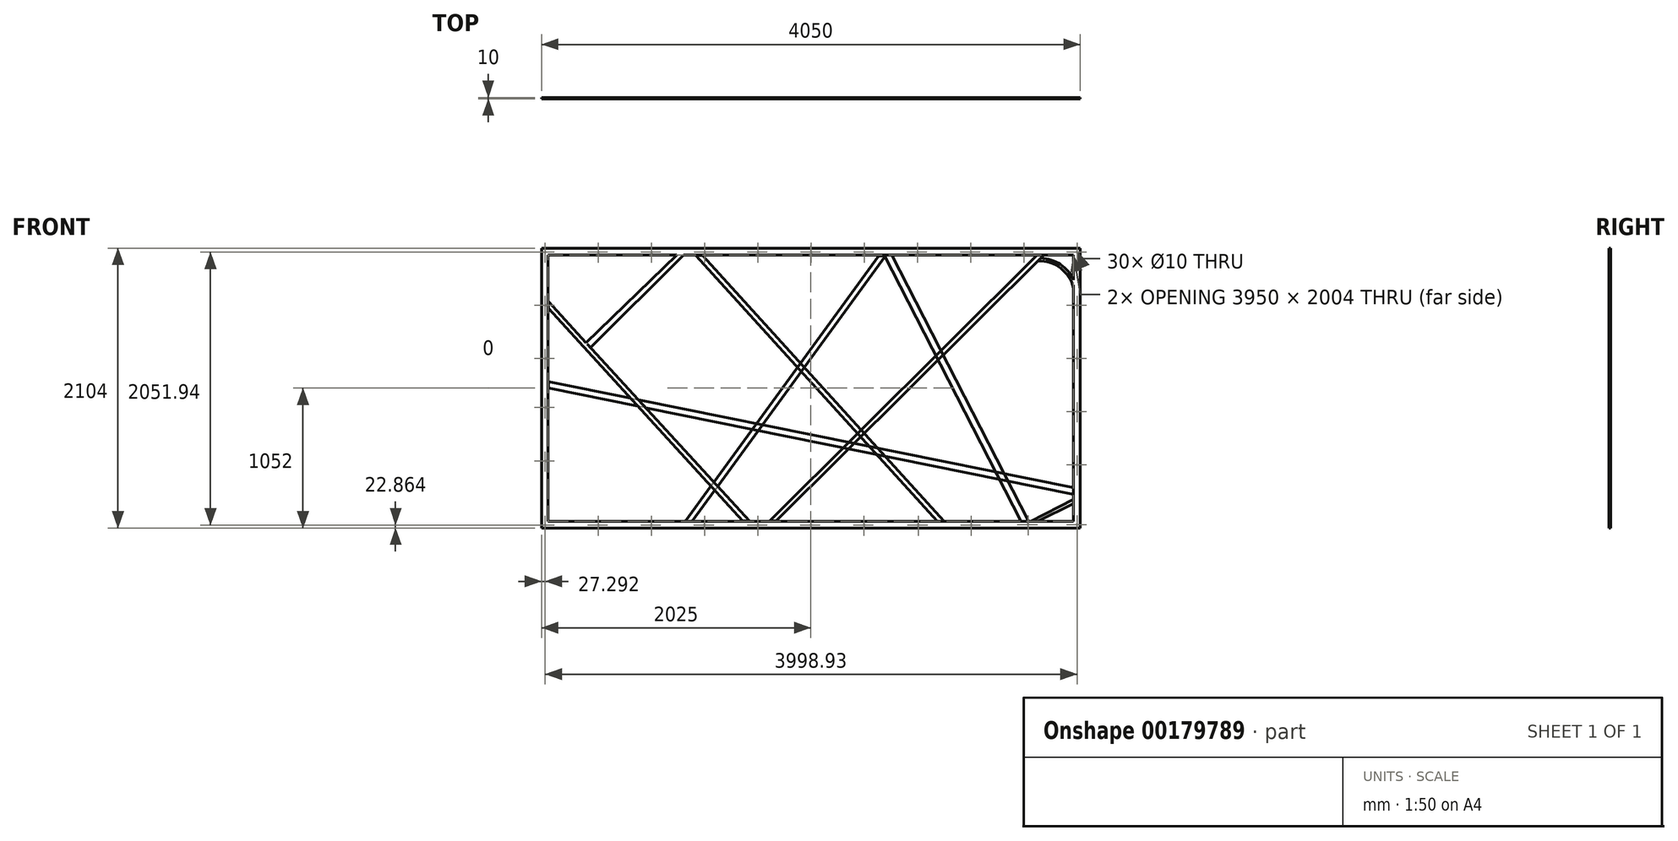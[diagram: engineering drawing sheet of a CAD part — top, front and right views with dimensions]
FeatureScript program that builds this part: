
annotation { "Feature Type Name" : "Feature", "Feature Type Description" : "" }
export const myFeature = defineFeature(function(context is Context, id is Id, definition is map)
    precondition{}
    {
        {
            var Q0;
            Q0=qCreatedBy(makeId("Front.planeOp"),FACE);
            var sketch = newSketch(context, id + "F0", { "sketchPlane" : qUnion([Q0])});
            skLineSegment(sketch, "E0.bottom", {"start": v(2025, -1052) * mm, "end": v(-2025, -1052) * mm});
            skLineSegment(sketch, "E0.top", {"start": v(2025, 1052) * mm, "end": v(-2025, 1052) * mm});
            skLineSegment(sketch, "E0.left", {"start": v(2025, -1052) * mm, "end": v(2025, 1052) * mm});
            skLineSegment(sketch, "E0.right", {"start": v(-2025, -1052) * mm, "end": v(-2025, 1052) * mm});
            skPoint(sketch, "E0.middle", {"position": v(0, 0) * mm});
            skLineSegment(sketch, "E1.bottom", {"start": v(1975, -1002) * mm, "end": v(-1975, -1002) * mm});
            skLineSegment(sketch, "E1.top", {"start": v(1975, 1002) * mm, "end": v(-1975, 1002) * mm});
            skLineSegment(sketch, "E1.left", {"start": v(1975, -1002) * mm, "end": v(1975, 1002) * mm});
            skLineSegment(sketch, "E1.right", {"start": v(-1975, -1002) * mm, "end": v(-1975, 1002) * mm});
            skSolve(sketch);
        }
        {
            var Q0;
            Q0 = qSketchRegion(id + "F0", true);
            extrude(context, id + "F1", {"entities" : qUnion([Q0]), "depth" : 5 * mm});
        }
        {
            var Q0;
            Q0=qCreatedBy(makeId("Front.planeOp"),FACE);
            var sketch = newSketch(context, id + "F2", { "sketchPlane" : qUnion([Q0])});
            skLineSegment(sketch, "E2", {"start": v(-1974.4, 0) * mm, "end": v(-1974.4, 50) * mm});
            skLineSegment(sketch, "E3", {"start": v(1976.4, -799.7) * mm, "end": v(1976.4, -749.7) * mm});
            skLineSegment(sketch, "E4", {"start": v(-1974.4, 50) * mm, "end": v(1976.4, -749.7) * mm});
            skLineSegment(sketch, "E5", {"start": v(1976.4, -799.7) * mm, "end": v(-1974.4, 0) * mm});
            skSolve(sketch);
        }
        {
            var Q0;
            Q0 = qSketchRegion(id + "F2", true);
            extrude(context, id + "F3", {"entities" : qUnion([Q0]), "depth" : 5 * mm});
        }
        {
            var Q0;
            Q0=qCreatedBy(makeId("Front.planeOp"),FACE);
            var sketch = newSketch(context, id + "F4", { "sketchPlane" : qUnion([Q0])});
            skLineSegment(sketch, "E6", {"start": v(-511.24, -998.6) * mm, "end": v(-461.24, -998.6) * mm});
            skLineSegment(sketch, "E7", {"start": v(-1974.4, 600.8) * mm, "end": v(-1974.4, 650.8) * mm});
            skLineSegment(sketch, "E8", {"start": v(-1974.4, 650.8) * mm, "end": v(-461.24, -998.6) * mm});
            skLineSegment(sketch, "E9", {"start": v(-511.24, -998.6) * mm, "end": v(-1974.4, 600.8) * mm});
            skSolve(sketch);
        }
        {
            var Q0;
            Q0 = qSketchRegion(id + "F4", true);
            extrude(context, id + "F5", {"entities" : qUnion([Q0]), "depth" : 5 * mm});
        }
        {
            var Q0;
            Q0=qCreatedBy(makeId("Front.planeOp"),FACE);
            var sketch = newSketch(context, id + "F6", { "sketchPlane" : qUnion([Q0])});
            skLineSegment(sketch, "E10", {"start": v(-1005.36, 1004.05) * mm, "end": v(-955.36, 1004.05) * mm});
            skLineSegment(sketch, "E11", {"start": v(-955.36, 1004.05) * mm, "end": v(-1654.99, 305) * mm});
            skLineSegment(sketch, "E12", {"start": v(-1654.99, 305) * mm, "end": v(-1690.33, 340.37) * mm});
            skLineSegment(sketch, "E13", {"start": v(-1690.33, 340.37) * mm, "end": v(-1005.36, 1004.05) * mm});
            skSolve(sketch);
        }
        {
            var Q0;
            Q0 = qSketchRegion(id + "F6", true);
            extrude(context, id + "F7", {"entities" : qUnion([Q0]), "operationType" : NewBodyOperationType.ADD, "depth" : 5 * mm});
        }
        {
            var Q0;
            Q0=qCreatedBy(makeId("Front.planeOp"),FACE);
            var sketch = newSketch(context, id + "F8", { "sketchPlane" : qUnion([Q0])});
            skLineSegment(sketch, "E14", {"start": v(-945.42, -1004.05) * mm, "end": v(-895.42, -1004.05) * mm});
            skLineSegment(sketch, "E15", {"start": v(509.56, 995.87) * mm, "end": v(559.56, 995.87) * mm});
            skLineSegment(sketch, "E16", {"start": v(559.56, 995.87) * mm, "end": v(-895.42, -1004.05) * mm});
            skLineSegment(sketch, "E17", {"start": v(-945.42, -1004.05) * mm, "end": v(509.56, 995.87) * mm});
            skSolve(sketch);
        }
        {
            var Q0;
            Q0 = qSketchRegion(id + "F8", true);
            extrude(context, id + "F9", {"entities" : qUnion([Q0]), "depth" : 5 * mm});
        }
        {
            var Q0;
            Q0=qCreatedBy(makeId("Front.planeOp"),FACE);
            var sketch = newSketch(context, id + "F10", { "sketchPlane" : qUnion([Q0])});
            skLineSegment(sketch, "E18", {"start": v(-310.57, -998.6) * mm, "end": v(-260.57, -998.6) * mm});
            skLineSegment(sketch, "E19", {"start": v(1702.97, 1004.05) * mm, "end": v(1752.97, 1004.05) * mm});
            skLineSegment(sketch, "E20", {"start": v(1752.97, 1004.05) * mm, "end": v(-260.57, -998.6) * mm});
            skLineSegment(sketch, "E21", {"start": v(-310.57, -998.6) * mm, "end": v(1702.97, 1004.05) * mm});
            skSolve(sketch);
        }
        {
            var Q0;
            Q0 = qSketchRegion(id + "F10", true);
            extrude(context, id + "F11", {"entities" : qUnion([Q0]), "depth" : 5 * mm});
        }
        {
            var Q0;
            Q0=qCreatedBy(makeId("Front.planeOp"),FACE);
            var sketch = newSketch(context, id + "F12", { "sketchPlane" : qUnion([Q0])});
            skLineSegment(sketch, "E22", {"start": v(1702.93, -1000.64) * mm, "end": v(1652.93, -1000.64) * mm});
            skLineSegment(sketch, "E23", {"start": v(1652.93, -1000.64) * mm, "end": v(1973.67, -836.48) * mm});
            skLineSegment(sketch, "E24", {"start": v(1973.67, -836.48) * mm, "end": v(1973.67, -867.16) * mm});
            skLineSegment(sketch, "E25", {"start": v(1973.67, -867.16) * mm, "end": v(1702.93, -1000.64) * mm});
            skSolve(sketch);
        }
        {
            var Q0;
            Q0 = qSketchRegion(id + "F12", true);
            extrude(context, id + "F13", {"entities" : qUnion([Q0]), "operationType" : NewBodyOperationType.ADD, "depth" : 5 * mm});
        }
        {
            var Q0;
            Q0=qCreatedBy(makeId("Front.planeOp"),FACE);
            var sketch = newSketch(context, id + "F14", { "sketchPlane" : qUnion([Q0])});
            skLineSegment(sketch, "E26", {"start": v(953.63, -1004.26) * mm, "end": v(1003.63, -1004.26) * mm});
            skLineSegment(sketch, "E27", {"start": v(-864.88, 999.74) * mm, "end": v(-814.88, 999.74) * mm});
            skLineSegment(sketch, "E28", {"start": v(-864.88, 999.74) * mm, "end": v(953.63, -1004.26) * mm});
            skLineSegment(sketch, "E29", {"start": v(1003.63, -1004.26) * mm, "end": v(-814.88, 999.74) * mm});
            skSolve(sketch);
        }
        {
            var Q0;
            Q0=makeQuery(id+"F14.imprint","IMPRINT",FACE,{"disambiguationData":[TD([[makeQuery(id+"F14.imprint","IMPRINT",EDGE,{"derivedFrom":sQuery(id+"F14.wireOp",EDGE,"E26")}),1.0]])]});
            extrude(context, id + "F15", {"entities" : qUnion([Q0]), "depth" : 5 * mm});
        }
        {
            var Q0;
            Q0=qCreatedBy(makeId("Front.planeOp"),FACE);
            var sketch = newSketch(context, id + "F16", { "sketchPlane" : qUnion([Q0])});
            skLineSegment(sketch, "E30", {"start": v(1581.92, -1004.26) * mm, "end": v(550.55, 1003.38) * mm});
            skLineSegment(sketch, "E31", {"start": v(550.55, 1003.38) * mm, "end": v(607.2, 1003.38) * mm});
            skLineSegment(sketch, "E32", {"start": v(607.2, 1003.38) * mm, "end": v(1638.18, -1003.51) * mm});
            skLineSegment(sketch, "E33", {"start": v(1638.18, -1003.51) * mm, "end": v(1581.92, -1004.26) * mm});
            skSolve(sketch);
        }
        {
            var Q0;
            Q0 = qSketchRegion(id + "F16", true);
            extrude(context, id + "F17", {"entities" : qUnion([Q0]), "depth" : 5 * mm});
        }
        {
            var Q0;
            Q0=qCreatedBy(makeId("Front.planeOp"),FACE);
            var sketch = newSketch(context, id + "F18", { "sketchPlane" : qUnion([Q0])});
            skArc(sketch, "E34", {"start": v(1975.78, 811.55) * mm, "mid": v(1876.04, 930.32) * mm, "end": v(1728.64, 978.55) * mm});
            skArc(sketch, "E35", {"start": v(1974.49, 752.4) * mm, "mid": v(1877.33, 902.78) * mm, "end": v(1706.84, 957.44) * mm});
            skLineSegment(sketch, "E36", {"start": v(1728.64, 978.55) * mm, "end": v(1706.84, 957.44) * mm});
            skLineSegment(sketch, "E37", {"start": v(1975.78, 811.55) * mm, "end": v(1974.49, 752.4) * mm});
            skSolve(sketch);
        }
        {
            var Q0;
            Q0 = qSketchRegion(id + "F18", true);
            extrude(context, id + "F19", {"entities" : qUnion([Q0]), "operationType" : NewBodyOperationType.ADD, "depth" : 5 * mm});
        }
        {
            var Q0;
            Q0=makeQuery(id+"F19.boolean.opBoolean","MERGE",FACE,{"derivedFrom":[makeQuery(id+"F11.opExtrude","CAP_FACE",FACE,{"disambiguationData":[OSD([sQuery(id+"F10.wireOp",EDGE,"E18"),sQuery(id+"F10.wireOp",EDGE,"E19"),sQuery(id+"F10.wireOp",EDGE,"E20"),sQuery(id+"F10.wireOp",EDGE,"E21")])],"isStart":false}),makeQuery(id+"F19.opExtrude","CAP_FACE",FACE,{"disambiguationData":[OSD([sQuery(id+"F18.wireOp",EDGE,"E34"),sQuery(id+"F18.wireOp",EDGE,"ZacZSDiB-RSxL-S7O9-GsN7-kvGr5qIdYWn7"),sQuery(id+"F18.wireOp",EDGE,"a9pKvjD8-VPx1-V8xl-zWNy-JQaimV4fLSww"),sQuery(id+"F18.wireOp",EDGE,"BgQaLwAU-geyg-JxmG-8WlX-JJudidIjWg7u")])],"isStart":false})]});
            var sketch = newSketch(context, id + "F20", { "sketchPlane" : qUnion([Q0])});
            skSolve(sketch);
        }
        {
            var Q0;
            Q0=makeQuery(id+"F20.imprint","IMPRINT",FACE,{"disambiguationData":[TD([[makeQuery(id+"F20.imprint","IMPRINT",EDGE,{"derivedFrom":makeQuery(id+"F19.opExtrude","CAP_EDGE",EDGE,{"disambiguationData":[OSD([sQuery(id+"F18.wireOp",EDGE,"E34")])],"isStart":false})}),1.0]])]});
            extrude(context, id + "F21", {"entities" : qUnion([Q0]), "depth" : 5 * mm});
        }
        {
            var Q0;
            Q0=qCreatedBy(makeId("Front.planeOp"),FACE);
            var sketch = newSketch(context, id + "F22", { "sketchPlane" : qUnion([Q0])});
            skLineSegment(sketch, "E38", {"start": v(-2026.02, 1022.8) * mm, "end": v(-1997.7, 1022.8) * mm});
            skLineSegment(sketch, "E39", {"start": v(-1997.7, 1022.8) * mm, "end": v(-1597.7, 1022.8) * mm});
            skLineSegment(sketch, "E40", {"start": v(-1597.7, 1022.8) * mm, "end": v(-1197.7, 1022.8) * mm});
            skLineSegment(sketch, "E41", {"start": v(-1197.7, 1022.8) * mm, "end": v(-797.7, 1022.8) * mm});
            skLineSegment(sketch, "E42", {"start": v(-797.7, 1022.8) * mm, "end": v(-397.7, 1022.8) * mm});
            skLineSegment(sketch, "E43", {"start": v(-397.7, 1022.8) * mm, "end": v(2.3, 1022.8) * mm});
            skLineSegment(sketch, "E44", {"start": v(2.3, 1022.8) * mm, "end": v(402.3, 1022.8) * mm});
            skLineSegment(sketch, "E45", {"start": v(402.3, 1022.8) * mm, "end": v(802.3, 1022.8) * mm});
            skLineSegment(sketch, "E46", {"start": v(802.3, 1022.8) * mm, "end": v(1202.3, 1022.8) * mm});
            skLineSegment(sketch, "E47", {"start": v(1202.3, 1022.8) * mm, "end": v(1602.3, 1022.8) * mm});
            skLineSegment(sketch, "E48", {"start": v(1602.3, 1022.8) * mm, "end": v(2001.22, 1022.8) * mm});
            skLineSegment(sketch, "E49", {"start": v(2001.22, 1022.8) * mm, "end": v(2001.22, 622.8) * mm});
            skLineSegment(sketch, "E50", {"start": v(2001.22, 622.8) * mm, "end": v(2001.22, 222.8) * mm});
            skLineSegment(sketch, "E51", {"start": v(2001.22, 222.8) * mm, "end": v(2001.22, -177.2) * mm});
            skLineSegment(sketch, "E52", {"start": v(2001.22, -177.2) * mm, "end": v(2001.22, -577.2) * mm});
            skLineSegment(sketch, "E53", {"start": v(2001.22, -577.2) * mm, "end": v(2001.22, -977.2) * mm});
            skLineSegment(sketch, "E54", {"start": v(2001.22, -977.2) * mm, "end": v(2001.22, -1026.04) * mm});
            skLineSegment(sketch, "E55", {"start": v(2001.22, -1026.04) * mm, "end": v(1632.52, -1026.04) * mm});
            skLineSegment(sketch, "E56", {"start": v(-1997.7, 1022.8) * mm, "end": v(-1997.7, 622.8) * mm});
            skLineSegment(sketch, "E57", {"start": v(-1997.7, 622.8) * mm, "end": v(-1997.7, 222.8) * mm});
            skLineSegment(sketch, "E58", {"start": v(-1997.7, 222.8) * mm, "end": v(-1997.7, -145.9) * mm});
            skLineSegment(sketch, "E59", {"start": v(-1997.7, -145.9) * mm, "end": v(-1997.7, -547.62) * mm});
            skLineSegment(sketch, "E60", {"start": v(-1997.7, -547.62) * mm, "end": v(-1997.7, -1029.14) * mm});
            skLineSegment(sketch, "E61", {"start": v(-1997.7, -1029.14) * mm, "end": v(-1597.77, -1029.14) * mm});
            skLineSegment(sketch, "E62", {"start": v(-1597.77, -1029.14) * mm, "end": v(-1198.8, -1029.14) * mm});
            skLineSegment(sketch, "E63", {"start": v(-1198.8, -1029.14) * mm, "end": v(-799.83, -1029.14) * mm});
            skLineSegment(sketch, "E64", {"start": v(-799.83, -1029.14) * mm, "end": v(-398.1, -1029.14) * mm});
            skLineSegment(sketch, "E65", {"start": v(-398.1, -1029.14) * mm, "end": v(0, -1029.14) * mm});
            skLineSegment(sketch, "E66", {"start": v(0, -1029.14) * mm, "end": v(399.84, -1029.14) * mm});
            skLineSegment(sketch, "E67", {"start": v(399.84, -1029.14) * mm, "end": v(807.06, -1029.14) * mm});
            skLineSegment(sketch, "E68", {"start": v(807.06, -1029.14) * mm, "end": v(1206.03, -1029.14) * mm});
            skCircle(sketch, "E69", {"center": v(-1997.7, 1022.8) * mm, "radius": 5 * mm});
            skCircle(sketch, "E70", {"center": v(-1597.7, 1022.8) * mm, "radius": 5 * mm});
            skCircle(sketch, "E71", {"center": v(-1197.7, 1022.8) * mm, "radius": 5 * mm});
            skSolve(sketch);
        }
        {
            var Q0;
            Q0=sQuery(id+"F22.wireOp",VERTEX,"E56.start");
            var Q1;
            Q1=sQuery(id+"F22.wireOp",VERTEX,"E70.center");
            var Q2;
            Q2=sQuery(id+"F22.wireOp",VERTEX,"E41.start");
            var Q3;
            Q3=sQuery(id+"F22.wireOp",VERTEX,"E57.start");
            var Q4;
            Q4=sQuery(id+"F22.wireOp",VERTEX,"E42.start");
            var Q5;
            Q5=sQuery(id+"F22.wireOp",VERTEX,"E43.start");
            var Q6;
            Q6=sQuery(id+"F22.wireOp",VERTEX,"E58.start");
            var Q7;
            Q7=sQuery(id+"F22.wireOp",VERTEX,"E44.start");
            var Q8;
            Q8=sQuery(id+"F22.wireOp",VERTEX,"E45.start");
            var Q9;
            Q9=sQuery(id+"F22.wireOp",VERTEX,"E45.end");
            var Q10;
            Q10=sQuery(id+"F22.wireOp",VERTEX,"E47.start");
            var Q11;
            Q11=sQuery(id+"F22.wireOp",VERTEX,"E48.start");
            var Q12;
            Q12=sQuery(id+"F22.wireOp",VERTEX,"E49.start");
            var Q13;
            Q13=sQuery(id+"F22.wireOp",VERTEX,"E50.start");
            var Q14;
            Q14=sQuery(id+"F22.wireOp",VERTEX,"E50.end");
            var Q15;
            Q15=sQuery(id+"F22.wireOp",VERTEX,"E51.end");
            var Q16;
            Q16=sQuery(id+"F22.wireOp",VERTEX,"E52.end");
            var Q17;
            Q17=sQuery(id+"F22.wireOp",VERTEX,"E55.start");
            var Q18;
            Q18=sQuery(id+"F22.wireOp",VERTEX,"E55.end");
            var Q19;
            Q19=sQuery(id+"F22.wireOp",VERTEX,"E68.end");
            var Q20;
            Q20=sQuery(id+"F22.wireOp",VERTEX,"E67.end");
            var Q21;
            Q21=sQuery(id+"F22.wireOp",VERTEX,"E67.start");
            var Q22;
            Q22=sQuery(id+"F22.wireOp",VERTEX,"E66.start");
            var Q23;
            Q23=sQuery(id+"F22.wireOp",VERTEX,"E65.start");
            var Q24;
            Q24=sQuery(id+"F22.wireOp",VERTEX,"E64.start");
            var Q25;
            Q25=sQuery(id+"F22.wireOp",VERTEX,"E63.start");
            var Q26;
            Q26=sQuery(id+"F22.wireOp",VERTEX,"E61.end");
            var Q27;
            Q27=sQuery(id+"F22.wireOp",VERTEX,"E60.end");
            var Q28;
            Q28=sQuery(id+"F22.wireOp",VERTEX,"E59.end");
            var Q29;
            Q29=sQuery(id+"F22.wireOp",VERTEX,"E58.end");
            var Q30;
            Q30=makeQuery(id+"F1.opExtrude","SWEPT_BODY",BODY,{"disambiguationData":[OSD([sQuery(id+"F0.wireOp",EDGE,"E0.bottom"),sQuery(id+"F0.wireOp",EDGE,"E0.top"),sQuery(id+"F0.wireOp",EDGE,"E0.left"),sQuery(id+"F0.wireOp",EDGE,"E0.right"),sQuery(id+"F0.wireOp",EDGE,"E1.bottom"),sQuery(id+"F0.wireOp",EDGE,"E1.top"),sQuery(id+"F0.wireOp",EDGE,"E1.left"),sQuery(id+"F0.wireOp",EDGE,"E1.right")])]});
            hole(context, id + "F23", {"style" : HoleStyle.SIMPLE, "endStyle" : HoleEndStyle.THROUGH, "oppositeDirection" : true, "holeDiameter" : 10 * mm, "locations" : qUnion([Q0, Q1, Q2, Q3, Q4, Q5, Q6, Q7, Q8, Q9, Q10, Q11, Q12, Q13, Q14, Q15, Q16, Q17, Q18, Q19, Q20, Q21, Q22, Q23, Q24, Q25, Q26, Q27, Q28, Q29]), "scope" : qUnion([Q30]), "isTappedThrough" : true});
        }
    });
